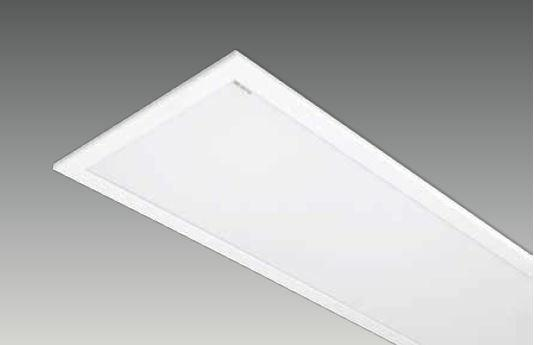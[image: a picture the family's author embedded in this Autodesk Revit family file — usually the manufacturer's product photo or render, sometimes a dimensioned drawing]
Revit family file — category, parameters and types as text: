
# Revit family: G 3012 OPL
name_source: partatom
category: Lighting Fixtures
revit_build: Autodesk Revit 2017 (Build: 20160225_1515(x64)
units: mm (PartAtom-declared; Revit-internal decimal feet)

## family parameters
Always vertical = Yes
Cut with Voids When Loaded = No
Host = Ceiling
Light Source = Yes
OmniClass Number = 23.80.70.11
OmniClass Title = Luminaries for Internal Lighting
Part Type = Normal
Room Calculation Point = No
Round Connector Dimension = Use Diameter
Shared = No

## types (2) — shared parameters
Color Filter = 16777215
Dimming Lamp Color Temperature Shift = <None>
Emit Shape Visible in Rendering = Yes
Emit from Rectangle Length = 1170 mm  [stored 3.83858 ft]
Emit from Rectangle Width = 270 mm  [stored 0.885827 ft]
Light Source Symbol Size = 610 mm
Manufacturer = ARLIGHT
Type Image = G 3012 OPL.JPG
Wattage Comments = 36

## type names (no varying parameters)
- GOPL.3012.36.30
- GOPL.3012.36.40

note: [stored X ft] marks values corroborated as IEEE doubles in the binary element streams (Revit-internal decimal feet)

## geometry (parser evidence)
native form markers: Sweep x2
no freeform markers — native parametric forms only
